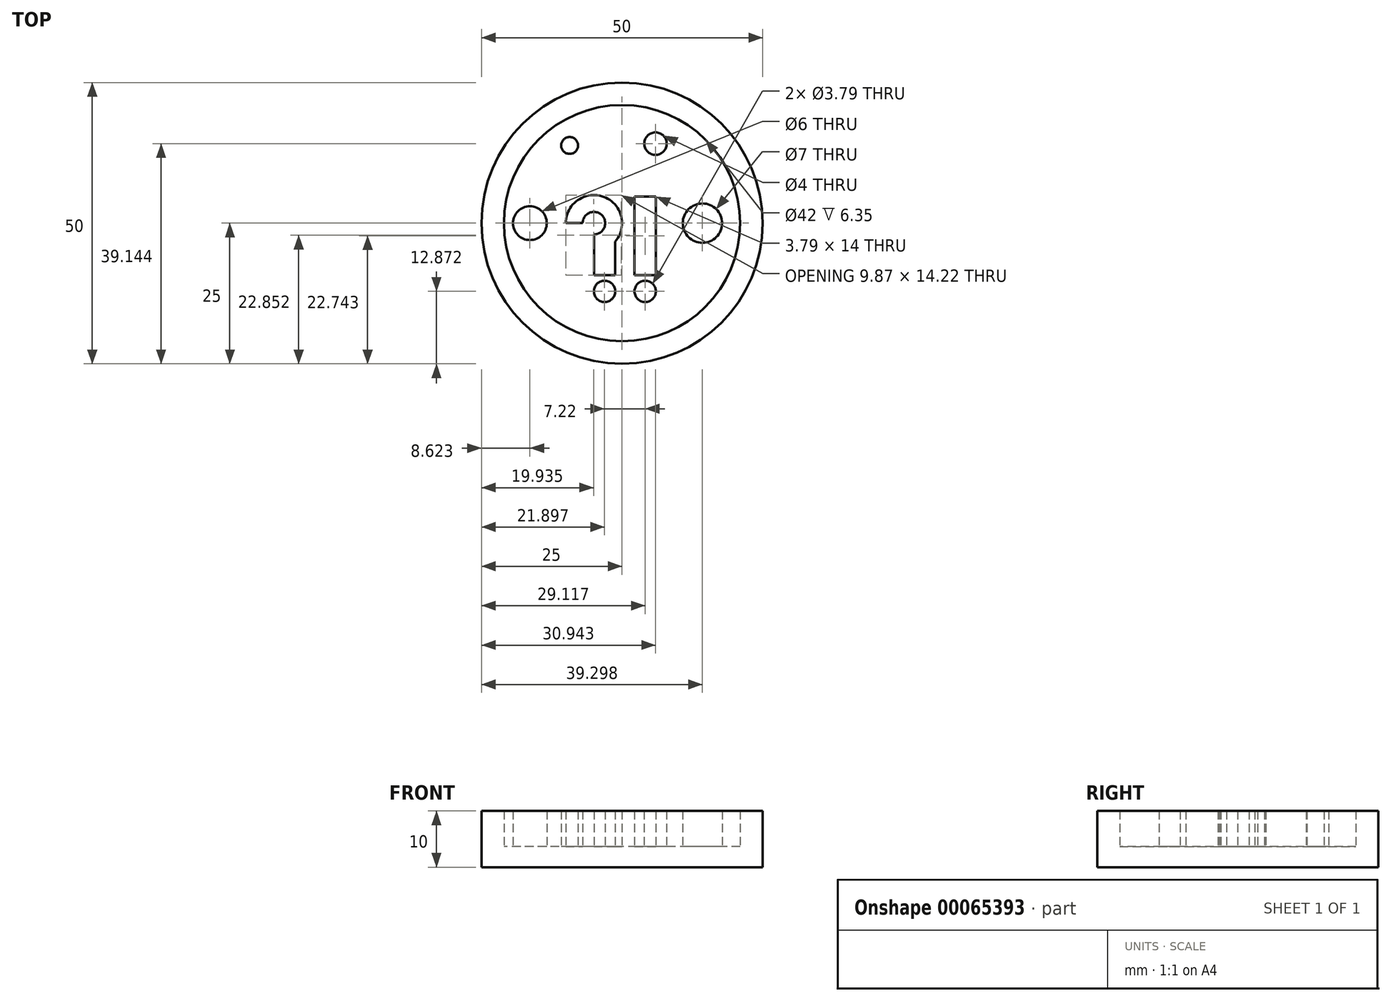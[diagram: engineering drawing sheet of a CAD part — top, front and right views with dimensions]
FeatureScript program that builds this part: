
annotation { "Feature Type Name" : "Feature", "Feature Type Description" : "" }
export const myFeature = defineFeature(function(context is Context, id is Id, definition is map)
    precondition{}
    {
        {
            var Q0;
            Q0=qCreatedBy(makeId("Top.planeOp"),FACE);
            var sketch = newSketch(context, id + "F0", { "sketchPlane" : qUnion([Q0])});
            skCircle(sketch, "E0", {"center": v(0, 0) * mm, "radius": 25 * mm});
            skSolve(sketch);
        }
        {
            var Q0;
            Q0 = qSketchRegion(id + "F0", true);
            extrude(context, id + "F1", {"entities" : qUnion([Q0]), "depth" : 10 * mm});
        }
        {
            var Q0;
            Q0=makeQuery(id+"F1.opExtrude","CAP_FACE",FACE,{"disambiguationData":[OSD([sQuery(id+"F0.wireOp",EDGE,"E0")])],"isStart":false});
            var sketch = newSketch(context, id + "F2", { "sketchPlane" : qUnion([Q0])});
            skCircle(sketch, "E1", {"center": v(0, 0) * mm, "radius": 21 * mm});
            skSolve(sketch);
        }
        {
            var Q0;
            Q0=makeQuery(id+"F2.imprint","IMPRINT",FACE,{"disambiguationData":[TD([[makeQuery(id+"F2.imprint","IMPRINT",EDGE,{"derivedFrom":sQuery(id+"F2.wireOp",EDGE,"E1")}),1.0]])]});
            extrude(context, id + "F3", {"entities" : qUnion([Q0]), "operationType" : NewBodyOperationType.REMOVE, "oppositeDirection" : true, "depth" : 6.35 * mm});
        }
        {
            var Q0;
            Q0=makeQuery(id+"F3.boolean.opBoolean","COPY",FACE,{"derivedFrom":makeQuery(id+"F3.opExtrude","CAP_FACE",FACE,{"disambiguationData":[OSD([sQuery(id+"F2.wireOp",EDGE,"E1")])],"isStart":false})});
            var sketch = newSketch(context, id + "F4", { "sketchPlane" : qUnion([Q0])});
            skArc(sketch, "E2", {"start": v(0, 0) * mm, "mid": v(-5, 5) * mm, "end": v(-10, 0) * mm});
            skArc(sketch, "E3", {"start": v(-3, 0) * mm, "mid": v(-5, 2) * mm, "end": v(-7, 0) * mm});
            skLineSegment(sketch, "E4", {"start": v(-10, 0) * mm, "end": v(-7, 0) * mm});
            skArc(sketch, "E5", {"start": v(-3, 0) * mm, "mid": v(-3.59, -1.41) * mm, "end": v(-5, -2) * mm});
            skLineSegment(sketch, "E6", {"start": v(-5, -2) * mm, "end": v(-5, -9.26) * mm});
            skLineSegment(sketch, "E7", {"start": v(-5, -9.26) * mm, "end": v(-1.2, -9.26) * mm});
            skLineSegment(sketch, "E8", {"start": v(-1.2, -9.26) * mm, "end": v(-1.2, -3.26) * mm});
            skPoint(sketch, "E9.center.orphan", {"position": v(0, 0) * mm});
            skArc(sketch, "E10", {"start": v(-1.2, -3.26) * mm, "mid": v(-0.31, -1.74) * mm, "end": v(0, 0) * mm});
            skLineSegment(sketch, "E11", {"start": v(2.22, 4.74) * mm, "end": v(2.22, -9.26) * mm});
            skLineSegment(sketch, "E12", {"start": v(2.22, -9.26) * mm, "end": v(6.01, -9.26) * mm});
            skLineSegment(sketch, "E13", {"start": v(6.01, -9.26) * mm, "end": v(6.01, 4.74) * mm});
            skLineSegment(sketch, "E14", {"start": v(2.22, 4.74) * mm, "end": v(6.01, 4.74) * mm});
            skCircle(sketch, "E15", {"center": v(4.12, -12.13) * mm, "radius": 1.9 * mm});
            skPoint(sketch, "E16", {"position": v(2.22, 4.74) * mm});
            skCircle(sketch, "E17", {"center": v(-3.1, -12.13) * mm, "radius": 1.9 * mm});
            skPoint(sketch, "E18.orphan", {"position": v(-5, 5) * mm});
            skCircle(sketch, "E19", {"center": v(-16.38, 0) * mm, "radius": 3 * mm});
            skCircle(sketch, "E20", {"center": v(14.3, 0) * mm, "radius": 3.5 * mm});
            skPoint(sketch, "E20.centerSnap0", {"position": v(-8.5, 0) * mm});
            skCircle(sketch, "E21", {"center": v(-9.31, 13.82) * mm, "radius": 1.5 * mm});
            skCircle(sketch, "E22", {"center": v(5.94, 14.14) * mm, "radius": 2 * mm});
            skLineSegment(sketch, "E23", {"start": v(-3.1, -14.02) * mm, "end": v(-3.1, -20.77) * mm, "construction": true});
            skLineSegment(sketch, "E24", {"start": v(4.12, -14.02) * mm, "end": v(4.12, -20.6) * mm, "construction": true});
            skLineSegment(sketch, "E25", {"start": v(17.8, 0) * mm, "end": v(21, 0) * mm, "construction": true});
            skLineSegment(sketch, "E26", {"start": v(14.3, -3.5) * mm, "end": v(14.3, -15.38) * mm, "construction": true});
            skLineSegment(sketch, "E27", {"start": v(-21, 0) * mm, "end": v(-19.38, 0) * mm, "construction": true});
            skLineSegment(sketch, "E28", {"start": v(-16.38, 3) * mm, "end": v(-16.38, 13.15) * mm, "construction": true});
            skLineSegment(sketch, "E29", {"start": v(-15.81, 13.82) * mm, "end": v(-10.81, 13.82) * mm, "construction": true});
            skLineSegment(sketch, "E30", {"start": v(-9.31, 15.32) * mm, "end": v(-9.31, 18.82) * mm, "construction": true});
            skLineSegment(sketch, "E31", {"start": v(7.94, 14.14) * mm, "end": v(15.52, 14.14) * mm, "construction": true});
            skLineSegment(sketch, "E32", {"start": v(5.94, 16.14) * mm, "end": v(5.94, 20.14) * mm, "construction": true});
            skText(sketch, "E33", { "text": "BIOE123 - TN", "fontName": "RobotoSlab-Regular.ttf"});
            skLineSegment(sketch, "E34", {"start": v(-10.4, -17.04) * mm, "end": v(-10.4, -18.24) * mm, "construction": true});
            skLineSegment(sketch, "E35", {"start": v(-10.4, -17.04) * mm, "end": v(-12.27, -17.04) * mm, "construction": true});
            skCircle(sketch, "E36", {"center": v(0, 0) * mm, "radius": 21 * mm});
            const initialGuessF4  = {"E33": [-0.0104, -0.01704, 1, 0, 0.0025]};
            skSetInitialGuess(sketch, initialGuessF4);
            skSolve(sketch);
        }
        {
            var Q0;
            Q0=makeQuery(id+"F4.imprint","IMPRINT",FACE,{"disambiguationData":[TD([[makeQuery(id+"F4.imprint","IMPRINT",EDGE,{"derivedFrom":sQuery(id+"F4.wireOp",EDGE,"E19")}),1.0]])]});
            var Q1;
            Q1=makeQuery(id+"F4.imprint","IMPRINT",FACE,{"disambiguationData":[TD([[makeQuery(id+"F4.imprint","IMPRINT",EDGE,{"derivedFrom":sQuery(id+"F4.wireOp",EDGE,"E2")}),1.0]])]});
            var Q2;
            Q2=makeQuery(id+"F4.imprint","IMPRINT",FACE,{"disambiguationData":[TD([[makeQuery(id+"F4.imprint","IMPRINT",EDGE,{"derivedFrom":sQuery(id+"F4.wireOp",EDGE,"E17")}),1.0]])]});
            var Q3;
            Q3=makeQuery(id+"F4.imprint","IMPRINT",FACE,{"disambiguationData":[TD([[makeQuery(id+"F4.imprint","IMPRINT",EDGE,{"derivedFrom":sQuery(id+"F4.wireOp",EDGE,"E15")}),1.0]])]});
            var Q4;
            Q4=makeQuery(id+"F4.imprint","IMPRINT",FACE,{"disambiguationData":[TD([[makeQuery(id+"F4.imprint","IMPRINT",EDGE,{"derivedFrom":sQuery(id+"F4.wireOp",EDGE,"E11")}),1.0]])]});
            var Q5;
            Q5=makeQuery(id+"F4.imprint","IMPRINT",FACE,{"disambiguationData":[TD([[makeQuery(id+"F4.imprint","IMPRINT",EDGE,{"derivedFrom":sQuery(id+"F4.wireOp",EDGE,"E20")}),1.0]])]});
            var Q6;
            Q6=makeQuery(id+"F4.imprint","IMPRINT",FACE,{"disambiguationData":[TD([[makeQuery(id+"F4.imprint","IMPRINT",EDGE,{"derivedFrom":sQuery(id+"F4.wireOp",EDGE,"E22")}),1.0]])]});
            var Q7;
            Q7=makeQuery(id+"F4.imprint","IMPRINT",FACE,{"disambiguationData":[TD([[makeQuery(id+"F4.imprint","IMPRINT",EDGE,{"derivedFrom":sQuery(id+"F4.wireOp",EDGE,"E21")}),1.0]])]});
            extrude(context, id + "F5", {"entities" : qUnion([Q0, Q1, Q2, Q3, Q4, Q5, Q6, Q7]), "operationType" : NewBodyOperationType.ADD, "depth" : 6.35 * mm});
        }
        {
            var Q0;
            Q0=makeQuery(id+"F3.boolean.opBoolean","COPY",FACE,{"derivedFrom":makeQuery(id+"F3.opExtrude","CAP_FACE",FACE,{"disambiguationData":[OSD([sQuery(id+"F2.wireOp",EDGE,"E1")])],"isStart":false})});
            extrude(context, id + "F6", {"entities" : qUnion([Q0]), "depth" : 6.35 * mm});
        }
    });
